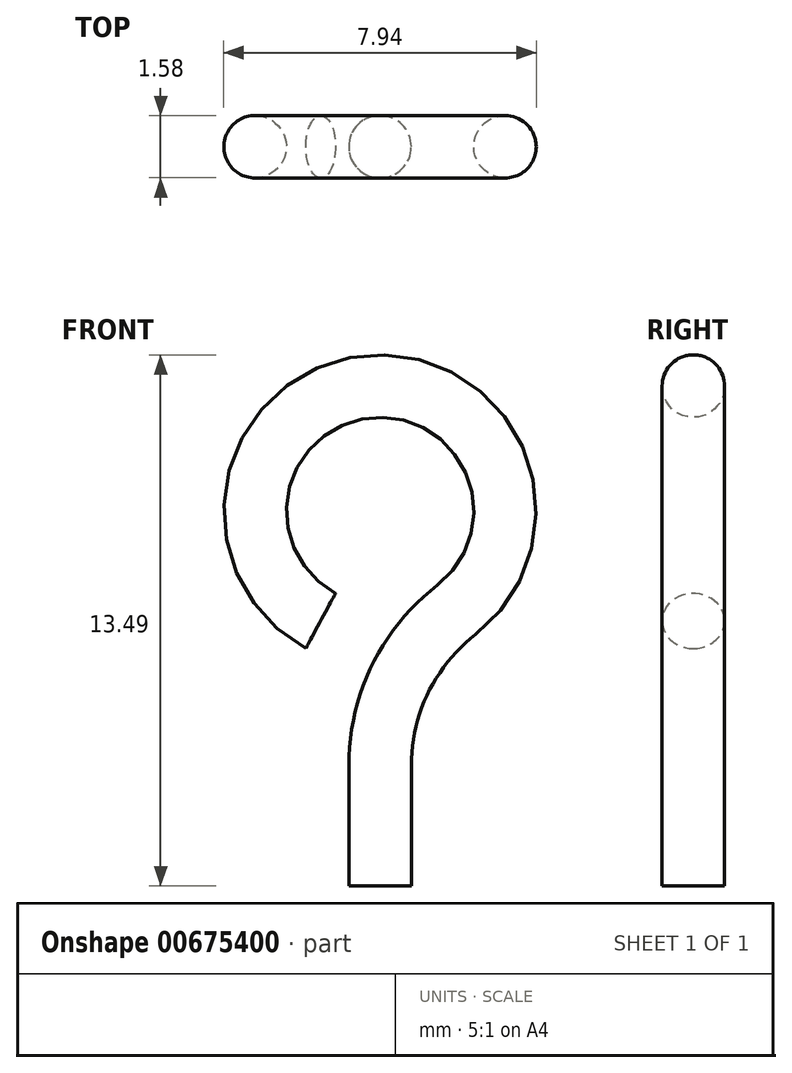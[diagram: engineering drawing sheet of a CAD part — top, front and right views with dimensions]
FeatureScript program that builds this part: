
annotation { "Feature Type Name" : "Feature", "Feature Type Description" : "" }
export const myFeature = defineFeature(function(context is Context, id is Id, definition is map)
    precondition{}
    {
        {
            var Q0;
            Q0=qCreatedBy(makeId("Front.planeOp"),FACE);
            var sketch = newSketch(context, id + "F0", { "sketchPlane" : qUnion([Q0])});
            skArc(sketch, "E0", {"start": v(1.94, 7.01) * mm, "mid": v(-0.26, 12.69) * mm, "end": v(-1.5, 6.73) * mm});
            skLineSegment(sketch, "E1", {"start": v(0, 3.06) * mm, "end": v(0, 0) * mm});
            skPoint(sketch, "E2.newPointA", {"position": v(0, 6.35) * mm});
            skArc(sketch, "E2.filletArc", {"start": v(1.94, 7.01) * mm, "mid": v(0.51, 5.26) * mm, "end": v(0, 3.06) * mm});
            skSolve(sketch);
        }
        {
            var Q0;
            Q0=qCreatedBy(makeId("Top.planeOp"),FACE);
            var sketch = newSketch(context, id + "F1", { "sketchPlane" : qUnion([Q0])});
            skCircle(sketch, "E3", {"center": v(0, 0) * mm, "radius": 0.8 * mm});
            skSolve(sketch);
        }
        {
            var Q0;
            Q0=makeQuery(id+"F1.imprint","IMPRINT",FACE,{"disambiguationData":[TD([[makeQuery(id+"F1.imprint","IMPRINT",EDGE,{"derivedFrom":sQuery(id+"F1.wireOp",EDGE,"E3")}),1.0]])]});
            var Q1;
            Q1=sQuery(id+"F0.wireOp",EDGE,"E1");
            var Q2;
            Q2=sQuery(id+"F0.wireOp",EDGE,"E2.filletArc");
            var Q3;
            Q3=sQuery(id+"F0.wireOp",EDGE,"E0");
            sweep(context, id + "F2", {"profiles" : qUnion([Q0]), "path" : qUnion([Q1, Q2, Q3])});
        }
    });
